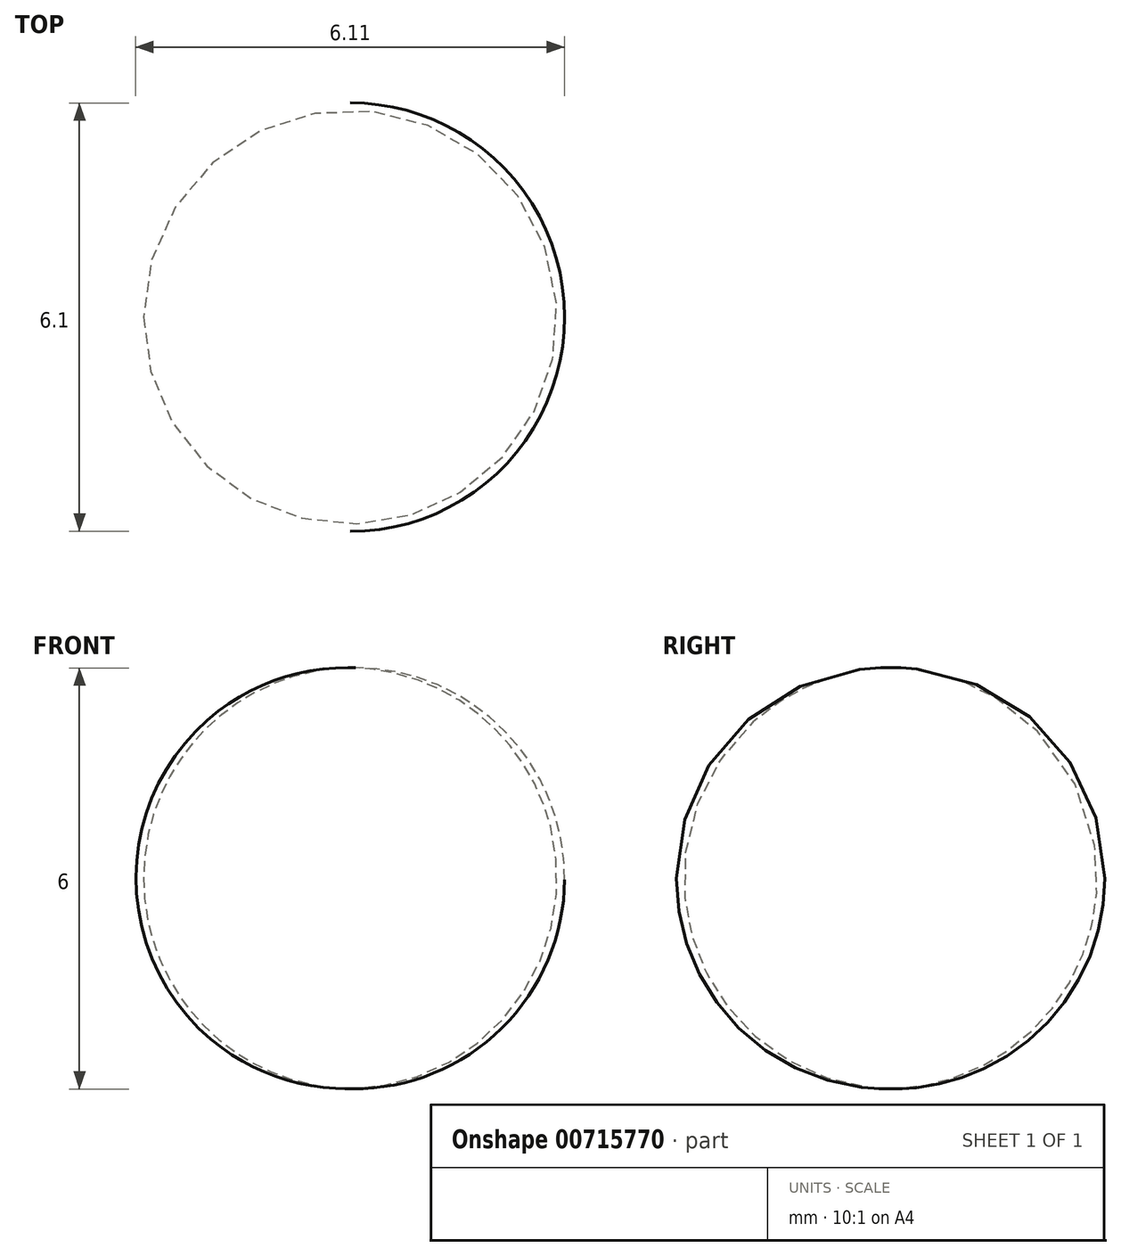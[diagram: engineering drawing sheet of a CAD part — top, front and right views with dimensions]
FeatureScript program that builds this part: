
annotation { "Feature Type Name" : "Feature", "Feature Type Description" : "" }
export const myFeature = defineFeature(function(context is Context, id is Id, definition is map)
    precondition{}
    {
        {
            var Q0;
            Q0=qCreatedBy(makeId("Front.planeOp"),FACE);
            var sketch = newSketch(context, id + "F0", { "sketchPlane" : qUnion([Q0])});
            skArc(sketch, "E0", {"start": v(-133.1, 43.61) * mm, "mid": v(-136.08, 40.63) * mm, "end": v(-133.15, 37.61) * mm});
            skLineSegment(sketch, "E1", {"start": v(-133.1, 43.61) * mm, "end": v(-133.15, 37.61) * mm});
            skSolve(sketch);
        }
        {
            var Q0;
            Q0=makeQuery(id+"F0.imprint","IMPRINT",FACE,{"disambiguationData":[TD([[makeQuery(id+"F0.imprint","IMPRINT",EDGE,{"derivedFrom":sQuery(id+"F0.wireOp",EDGE,"E0")}),1.0]])]});
            var Q1;
            Q1=sQuery(id+"F0.wireOp",EDGE,"E1");
            revolve(context, id + "F1", {"surfaceOperationType" : NewSurfaceOperationType.NEW, "entities" : qUnion([Q0]), "axis" : qUnion([Q1]), "revolveType" : RevolveType.FULL});
        }
    });
